# Revit family: Grohe_WCSeat_BauCeramic_39492000
name_source: partatom
category: Plumbing Fixtures
units: mm (PartAtom-declared; Revit-internal decimal feet)

## family parameters
Cut with Voids When Loaded = No
Host = Face
OmniClass Number = 23.45.05.00
OmniClass Title = Sanitary Equipment
Part Type = Normal
Room Calculation Point = No
Round Connector Dimension = Use Diameter
Shared = No

## types (1)
- BAU CERAMIC WC Seat (39492000)
    Assembly Code = D2041
    AssetType = Fixed
    BIMObjectName = Grohe_WCSeat_BauCeramic_39492000
    CO2NeutralProduction = GROHE is one of the first leading manufacturer within the sanitary industry having a CO2-neutral production.
    ClassificationName = Uniclass2015
    ClassificationValue = Pr_40_20_93_95
    Color = White
    Cost = 0 $
    Default Elevation = 1219 mm
    Description = BAU CERAMIC WC Seat
    DimensionsDocumentLink = https://cdn.cloud.grohe.com
    DocumentationCertificates = https://www.bimstore.co
    DocumentationInstallationGuide = https://www.bimstore.co
    DocumentationLiterature = https://www.bimstore.co
    DocumentationMaintenance = https://www.bimstore.co
    DocumentationTechnical = https://www.bimstore.co
    DurationUnit = Years
    EF000007 = White
    EF000116 = 0
    EF001187 = true
    EF001251 = false
    EF011715 = 0
    EF021451 = false
    EF022411 = false
    EF023159 = 0
    EF023790 = false
    EF023826 = true
    EF023827 = not relevant
    EF023829 = false
    EF023830 = true
    EF023831 = false
    EF023832 = true
    EF023833 = Stainless steel
    EF023835 = Duroplast
    EF023836 = not relevant
    EF023870 = false
    EF023892 = Pins inserted In lid
    EF023893 = false
    EF024897 = Other
    Ecojoy = No
    ExpectedLife = 0
    FullRecyclabilityOfPlastic = All plastic components are fully recycable
    GROHESocialCommittment = green.grohe.com/social_engagement
    GROHESustainability = green.grohe.com
    IfcExportAs = IfcPipeFitting
    IfcExportType = IfcPipeFittingType
    Keynote = N44
    Manufacturer = Grohe
    ManufacturerName = Grohe
    Model = BAU CERAMIC WC Seat
    ModelNumber = 39492000
    ModelReference = BAU CERAMIC WC Seat
    NBSDescription = WC seats and covers
    NBSObjectName = Grohe - WC seats and covers
    NBSReference = 45-35-70/391
    NominalDepth = 0 mm  [stored 0 ft]
    NominalHeight = 0 mm  [stored 0 ft]
    NominalLength = 0 mm  [stored 0 ft]
    PrimaryMaterial = Grohe_White
    ProductDescription = with lid

quick release function

detachable

material: Duroplast

including fixation set

stainless steel hinges

easy fixation from above

weight bearing capacity 150 kg

compatible with all Bau Ceramic bowls except 39 910 000
    ProductNumber = 39492000
    ProductShortText = BAU CERAMIC WC Seat
    ProductType = WCs + Urinals
    ProductionYear = 2023
    SecondaryMaterial = Grohe_Chrome
    SustainabilityAward = green.grohe.com/awards
    SustainabilityReport = green.grohe.com/reporting
    TPIDocumentLink = https://cdn.cloud.grohe.com
    Type Comments = BAU CERAMIC WC Seat
    TypeName = BAU CERAMIC WC Seat
    URL = https://www.grohe.co.uk
    WarrantyDurationLabor = 0
    WarrantyDurationParts = 0
    WarrantyDurationUnit = Years
    _BSBibleVersion = 17
    _BimSpecGuid = 0
    _CurrentRevision = 1
    _DistributedBy = https://www.bimstore.co
    _ObjectUserGuide = https://www.bimstore.co

note: [stored X ft] marks values corroborated as IEEE doubles in the binary element streams (Revit-internal decimal feet)

## geometry (parser evidence)
native form markers: Sweep x2
no freeform markers — native parametric forms only
